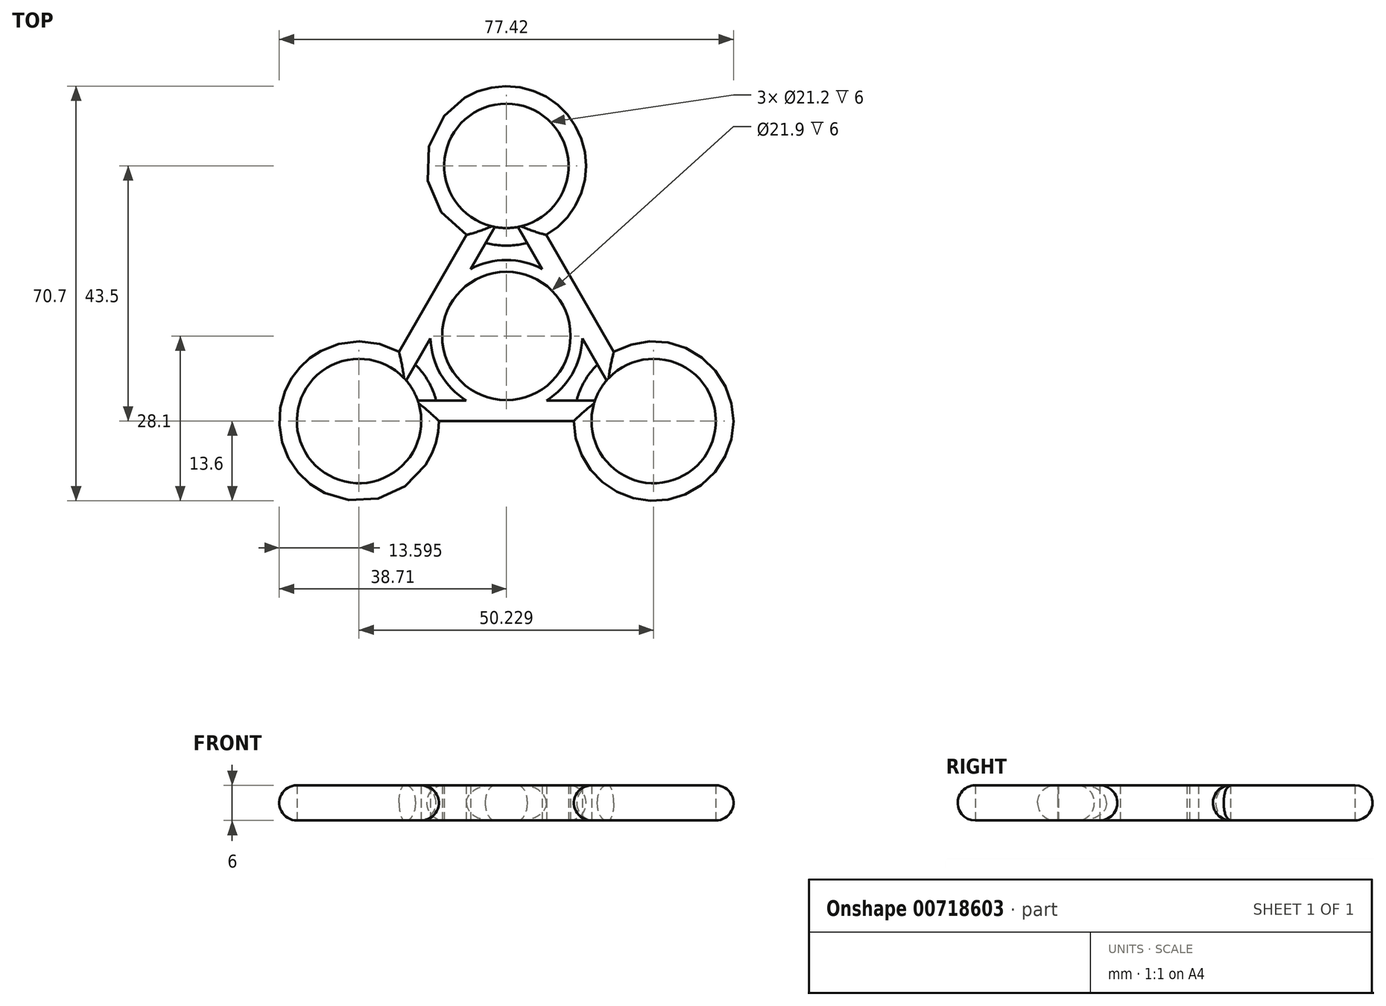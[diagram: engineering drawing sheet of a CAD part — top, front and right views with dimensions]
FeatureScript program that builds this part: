
annotation { "Feature Type Name" : "Feature", "Feature Type Description" : "" }
export const myFeature = defineFeature(function(context is Context, id is Id, definition is map)
    precondition{}
    {
        {
            var Q0;
            Q0=qCreatedBy(makeId("Top.planeOp"),FACE);
            var sketch = newSketch(context, id + "F0", { "sketchPlane" : qUnion([Q0])});
            skCircle(sketch, "E0", {"center": v(0, 0) * mm, "radius": 10.95 * mm});
            skCircle(sketch, "E1.cCircle", {"center": v(0, 0) * mm, "radius": 14.5 * mm, "construction": true});
            skLineSegment(sketch, "E1.0", {"start": v(0, 29) * mm, "end": v(25.11, -14.5) * mm});
            skLineSegment(sketch, "E1.1", {"start": v(25.11, -14.5) * mm, "end": v(-25.11, -14.5) * mm});
            skLineSegment(sketch, "E1.2", {"start": v(-25.11, -14.5) * mm, "end": v(0, 29) * mm});
            skPoint(sketch, "E1.0.midPoint", {"position": v(12.56, 7.25) * mm});
            skCircle(sketch, "E2", {"center": v(0, 29) * mm, "radius": 10.6 * mm});
            skCircle(sketch, "E3", {"center": v(25.11, -14.5) * mm, "radius": 10.6 * mm});
            skCircle(sketch, "E4", {"center": v(-25.11, -14.5) * mm, "radius": 10.6 * mm});
            skCircle(sketch, "E5.0", {"center": v(0, 29) * mm, "radius": 13.6 * mm});
            skCircle(sketch, "E6.0", {"center": v(-25.11, -14.5) * mm, "radius": 13.6 * mm});
            skCircle(sketch, "E7.0", {"center": v(25.11, -14.5) * mm, "radius": 13.6 * mm});
            skLineSegment(sketch, "E8.0", {"start": v(-2.35, 26.06) * mm, "end": v(22.16, -16.39) * mm});
            skLineSegment(sketch, "E9.0", {"start": v(-21.4, -15.06) * mm, "end": v(3.11, 27.39) * mm});
            skLineSegment(sketch, "E10.0", {"start": v(23.75, -11) * mm, "end": v(-25.27, -11) * mm});
            skCircle(sketch, "E11.0", {"center": v(0, 0) * mm, "radius": 12.95 * mm});
            skSolve(sketch);
        }
        {
            var Q0;
            Q0 = qSketchRegion(id + "F0", true);
            var Q1;
            {var subQ0=sQuery(id+"F0.wireOp",EDGE,"E10.0");var subQ1=sQuery(id+"F0.wireOp",EDGE,"E4");var subQ2=makeQuery(id+"F0.imprint","INTERSECT",VERTEX,{"derivedFrom":[subQ1,subQ0]});Q1=makeQuery(id+"F0.imprint","IMPRINT",FACE,{"disambiguationData":[TD([[makeQuery(id+"F0.imprint","IMPRINT",EDGE,{"disambiguationData":[TD([[subQ2,-1.0]])],"derivedFrom":subQ1}),-1.0]])]});}
            var Q2;
            {var subQ0=sQuery(id+"F0.wireOp",EDGE,"E8.0");var subQ1=sQuery(id+"F0.wireOp",EDGE,"E3");var subQ2=makeQuery(id+"F0.imprint","INTERSECT",VERTEX,{"derivedFrom":[subQ1,subQ0]});Q2=makeQuery(id+"F0.imprint","IMPRINT",FACE,{"disambiguationData":[TD([[makeQuery(id+"F0.imprint","IMPRINT",EDGE,{"disambiguationData":[TD([[subQ2,-1.0]])],"derivedFrom":subQ1}),-1.0]])]});}
            var Q3;
            {var subQ0=sQuery(id+"F0.wireOp",EDGE,"E8.0");var subQ1=sQuery(id+"F0.wireOp",EDGE,"E0");var subQ2=makeQuery(id+"F0.imprint","INTERSECT",VERTEX,{"disambiguationData":[OD(1.0)],"derivedFrom":[subQ1,subQ0]});Q3=makeQuery(id+"F0.imprint","IMPRINT",FACE,{"disambiguationData":[TD([[makeQuery(id+"F0.imprint","IMPRINT",EDGE,{"disambiguationData":[TD([[subQ2,1.0]])],"derivedFrom":subQ1}),-1.0]])]});}
            var Q4;
            {var subQ0=sQuery(id+"F0.wireOp",EDGE,"E9.0");var subQ1=sQuery(id+"F0.wireOp",EDGE,"E0");var subQ2=makeQuery(id+"F0.imprint","INTERSECT",VERTEX,{"disambiguationData":[OD(1.0)],"derivedFrom":[subQ1,subQ0]});Q4=makeQuery(id+"F0.imprint","IMPRINT",FACE,{"disambiguationData":[TD([[makeQuery(id+"F0.imprint","IMPRINT",EDGE,{"disambiguationData":[TD([[subQ2,-1.0]])],"derivedFrom":subQ1}),-1.0]])]});}
            var Q5;
            {var subQ0=sQuery(id+"F0.wireOp",EDGE,"E8.0");var subQ1=sQuery(id+"F0.wireOp",EDGE,"E0");var subQ2=makeQuery(id+"F0.imprint","INTERSECT",VERTEX,{"disambiguationData":[OD(0.0)],"derivedFrom":[subQ1,subQ0]});Q5=makeQuery(id+"F0.imprint","IMPRINT",FACE,{"disambiguationData":[TD([[makeQuery(id+"F0.imprint","IMPRINT",EDGE,{"disambiguationData":[TD([[subQ2,-1.0]])],"derivedFrom":subQ1}),-1.0]])]});}
            var Q6;
            {var subQ0=sQuery(id+"F0.wireOp",EDGE,"E9.0");var subQ1=sQuery(id+"F0.wireOp",EDGE,"E2");var subQ2=makeQuery(id+"F0.imprint","INTERSECT",VERTEX,{"derivedFrom":[subQ1,subQ0]});Q6=makeQuery(id+"F0.imprint","IMPRINT",FACE,{"disambiguationData":[TD([[makeQuery(id+"F0.imprint","IMPRINT",EDGE,{"disambiguationData":[TD([[subQ2,-1.0]])],"derivedFrom":subQ1}),-1.0]])]});}
            var Q7;
            {var subQ0=sQuery(id+"F0.wireOp",EDGE,"E9.0");var subQ1=sQuery(id+"F0.wireOp",EDGE,"E0");var subQ2=makeQuery(id+"F0.imprint","INTERSECT",VERTEX,{"disambiguationData":[OD(0.0)],"derivedFrom":[subQ1,subQ0]});Q7=makeQuery(id+"F0.imprint","IMPRINT",FACE,{"disambiguationData":[TD([[makeQuery(id+"F0.imprint","IMPRINT",EDGE,{"disambiguationData":[TD([[subQ2,-1.0]])],"derivedFrom":subQ1}),-1.0]])]});}
            var Q8;
            {var subQ0=sQuery(id+"F0.wireOp",EDGE,"E10.0");var subQ1=sQuery(id+"F0.wireOp",EDGE,"E0");var subQ2=makeQuery(id+"F0.imprint","INTERSECT",VERTEX,{"disambiguationData":[OD(0.0)],"derivedFrom":[subQ1,subQ0]});Q8=makeQuery(id+"F0.imprint","IMPRINT",FACE,{"disambiguationData":[TD([[makeQuery(id+"F0.imprint","IMPRINT",EDGE,{"disambiguationData":[TD([[subQ2,-1.0]])],"derivedFrom":subQ1}),-1.0]])]});}
            var Q9;
            {var subQ0=sQuery(id+"F0.wireOp",EDGE,"E8.0");var subQ1=sQuery(id+"F0.wireOp",EDGE,"E0");var subQ2=makeQuery(id+"F0.imprint","INTERSECT",VERTEX,{"disambiguationData":[OD(0.0)],"derivedFrom":[subQ1,subQ0]});Q9=makeQuery(id+"F0.imprint","IMPRINT",FACE,{"disambiguationData":[TD([[makeQuery(id+"F0.imprint","IMPRINT",EDGE,{"disambiguationData":[TD([[subQ2,1.0]])],"derivedFrom":subQ1}),-1.0]])]});}
            var Q10;
            {var subQ0=sQuery(id+"F0.wireOp",EDGE,"E11.0");var subQ1=sQuery(id+"F0.wireOp",EDGE,"E8.0");var subQ2=makeQuery(id+"F0.imprint","INTERSECT",VERTEX,{"disambiguationData":[OD(0.0)],"derivedFrom":[subQ1,subQ0]});Q10=makeQuery(id+"F0.imprint","IMPRINT",FACE,{"disambiguationData":[TD([[makeQuery(id+"F0.imprint","IMPRINT",EDGE,{"disambiguationData":[TD([[subQ2,-1.0]])],"derivedFrom":subQ1}),1.0]])]});}
            var Q11;
            Q11=makeQuery(id+"F0.imprint","IMPRINT",FACE,{"disambiguationData":[TD([[makeQuery(id+"F0.imprint","IMPRINT",EDGE,{"derivedFrom":sQuery(id+"F0.wireOp",EDGE,"E0")}),-1.0]])]});
            var Q12;
            {var subQ0=sQuery(id+"F0.wireOp",EDGE,"E11.0");var subQ1=sQuery(id+"F0.wireOp",EDGE,"E9.0");var subQ2=makeQuery(id+"F0.imprint","INTERSECT",VERTEX,{"disambiguationData":[OD(0.0)],"derivedFrom":[subQ1,subQ0]});Q12=makeQuery(id+"F0.imprint","IMPRINT",FACE,{"disambiguationData":[TD([[makeQuery(id+"F0.imprint","IMPRINT",EDGE,{"disambiguationData":[TD([[subQ2,-1.0]])],"derivedFrom":subQ1}),1.0]])]});}
            var Q13;
            {var subQ0=sQuery(id+"F0.wireOp",EDGE,"E11.0");var subQ1=sQuery(id+"F0.wireOp",EDGE,"E10.0");var subQ2=makeQuery(id+"F0.imprint","INTERSECT",VERTEX,{"disambiguationData":[OD(0.0)],"derivedFrom":[subQ1,subQ0]});Q13=makeQuery(id+"F0.imprint","IMPRINT",FACE,{"disambiguationData":[TD([[makeQuery(id+"F0.imprint","IMPRINT",EDGE,{"disambiguationData":[TD([[subQ2,-1.0]])],"derivedFrom":subQ1}),1.0]])]});}
            extrude(context, id + "F1", {"entities" : qUnion([Q0, Q1, Q2, Q3, Q4, Q5, Q6, Q7, Q8, Q9, Q10, Q11, Q12, Q13]), "depth" : 6 * mm, "offsetDistance" : 25 * mm});
        }
        {
            var Q0;
            {var subQ0=sQuery(id+"F0.wireOp",EDGE,"E6.0");Q0=makeQuery(id+"F1.opExtrude","CAP_EDGE",EDGE,{"disambiguationData":[OSD([subQ0]),TDD([makeQuery(id+"F0.imprint","IMPRINT",EDGE,{"disambiguationData":[TD([[makeQuery(id+"F0.imprint","INTERSECT",VERTEX,{"derivedFrom":[sQuery(id+"F0.wireOp",EDGE,"E1.1"),subQ0]}),1.0]])],"derivedFrom":subQ0})])],"isStart":false});}
            var Q1;
            {var subQ0=sQuery(id+"F0.wireOp",EDGE,"E7.0");Q1=makeQuery(id+"F1.opExtrude","CAP_EDGE",EDGE,{"disambiguationData":[OSD([subQ0]),TDD([makeQuery(id+"F0.imprint","IMPRINT",EDGE,{"disambiguationData":[TD([[makeQuery(id+"F0.imprint","INTERSECT",VERTEX,{"derivedFrom":[sQuery(id+"F0.wireOp",EDGE,"E1.0"),subQ0]}),1.0]])],"derivedFrom":subQ0})])],"isStart":false});}
            var Q2;
            {var subQ0=sQuery(id+"F0.wireOp",EDGE,"E5.0");Q2=makeQuery(id+"F1.opExtrude","CAP_EDGE",EDGE,{"disambiguationData":[OSD([subQ0]),TDD([makeQuery(id+"F0.imprint","IMPRINT",EDGE,{"disambiguationData":[TD([[makeQuery(id+"F0.imprint","INTERSECT",VERTEX,{"derivedFrom":[sQuery(id+"F0.wireOp",EDGE,"E1.0"),subQ0]}),-1.0]])],"derivedFrom":subQ0})])],"isStart":false});}
            var Q3;
            Q3=makeQuery(id+"F1.opExtrude","CAP_EDGE",EDGE,{"disambiguationData":[OSD([sQuery(id+"F0.wireOp",EDGE,"E1.1")])],"isStart":false});
            var Q4;
            Q4=makeQuery(id+"F1.opExtrude","CAP_EDGE",EDGE,{"disambiguationData":[OSD([sQuery(id+"F0.wireOp",EDGE,"E1.0")])],"isStart":false});
            var Q5;
            Q5=makeQuery(id+"F1.opExtrude","CAP_EDGE",EDGE,{"disambiguationData":[OSD([sQuery(id+"F0.wireOp",EDGE,"E1.2")])],"isStart":false});
            var Q6;
            {var subQ0=sQuery(id+"F0.wireOp",EDGE,"E6.0");Q6=makeQuery(id+"F1.opExtrude","CAP_EDGE",EDGE,{"disambiguationData":[OSD([subQ0]),TDD([makeQuery(id+"F0.imprint","IMPRINT",EDGE,{"disambiguationData":[TD([[makeQuery(id+"F0.imprint","INTERSECT",VERTEX,{"derivedFrom":[subQ0,sQuery(id+"F0.wireOp",EDGE,"E10.0")]}),-1.0]])],"derivedFrom":subQ0})])],"isStart":false});}
            var Q7;
            {var subQ0=sQuery(id+"F0.wireOp",EDGE,"E6.0");Q7=makeQuery(id+"F1.opExtrude","CAP_EDGE",EDGE,{"disambiguationData":[OSD([subQ0]),TDD([makeQuery(id+"F0.imprint","IMPRINT",EDGE,{"disambiguationData":[TD([[makeQuery(id+"F0.imprint","INTERSECT",VERTEX,{"derivedFrom":[sQuery(id+"F0.wireOp",EDGE,"E1.1"),subQ0]}),1.0]])],"derivedFrom":subQ0})])],"isStart":true});}
            var Q8;
            Q8=makeQuery(id+"F1.opExtrude","CAP_EDGE",EDGE,{"disambiguationData":[OSD([sQuery(id+"F0.wireOp",EDGE,"E1.1")])],"isStart":true});
            var Q9;
            {var subQ0=sQuery(id+"F0.wireOp",EDGE,"E7.0");Q9=makeQuery(id+"F1.opExtrude","CAP_EDGE",EDGE,{"disambiguationData":[OSD([subQ0]),TDD([makeQuery(id+"F0.imprint","IMPRINT",EDGE,{"disambiguationData":[TD([[makeQuery(id+"F0.imprint","INTERSECT",VERTEX,{"derivedFrom":[sQuery(id+"F0.wireOp",EDGE,"E1.0"),subQ0]}),1.0]])],"derivedFrom":subQ0})])],"isStart":true});}
            var Q10;
            Q10=makeQuery(id+"F1.opExtrude","CAP_EDGE",EDGE,{"disambiguationData":[OSD([sQuery(id+"F0.wireOp",EDGE,"E1.0")])],"isStart":true});
            var Q11;
            {var subQ0=sQuery(id+"F0.wireOp",EDGE,"E5.0");Q11=makeQuery(id+"F1.opExtrude","CAP_EDGE",EDGE,{"disambiguationData":[OSD([subQ0]),TDD([makeQuery(id+"F0.imprint","IMPRINT",EDGE,{"disambiguationData":[TD([[makeQuery(id+"F0.imprint","INTERSECT",VERTEX,{"derivedFrom":[sQuery(id+"F0.wireOp",EDGE,"E1.0"),subQ0]}),-1.0]])],"derivedFrom":subQ0})])],"isStart":true});}
            var Q12;
            Q12=makeQuery(id+"F1.opExtrude","CAP_EDGE",EDGE,{"disambiguationData":[OSD([sQuery(id+"F0.wireOp",EDGE,"E1.2")])],"isStart":true});
            var Q13;
            {var subQ0=sQuery(id+"F0.wireOp",EDGE,"E7.0");Q13=makeQuery(id+"F1.opExtrude","CAP_EDGE",EDGE,{"disambiguationData":[OSD([subQ0]),TDD([makeQuery(id+"F0.imprint","IMPRINT",EDGE,{"disambiguationData":[TD([[makeQuery(id+"F0.imprint","INTERSECT",VERTEX,{"derivedFrom":[subQ0,sQuery(id+"F0.wireOp",EDGE,"E8.0")]}),-1.0]])],"derivedFrom":subQ0})])],"isStart":false});}
            var Q14;
            {var subQ0=sQuery(id+"F0.wireOp",EDGE,"E5.0");Q14=makeQuery(id+"F1.opExtrude","CAP_EDGE",EDGE,{"disambiguationData":[OSD([subQ0]),TDD([makeQuery(id+"F0.imprint","IMPRINT",EDGE,{"disambiguationData":[TD([[makeQuery(id+"F0.imprint","INTERSECT",VERTEX,{"derivedFrom":[subQ0,sQuery(id+"F0.wireOp",EDGE,"E9.0")]}),-1.0]])],"derivedFrom":subQ0})])],"isStart":false});}
            var Q15;
            {var subQ0=sQuery(id+"F0.wireOp",EDGE,"E5.0");Q15=makeQuery(id+"F1.opExtrude","CAP_EDGE",EDGE,{"disambiguationData":[OSD([subQ0]),TDD([makeQuery(id+"F0.imprint","IMPRINT",EDGE,{"disambiguationData":[TD([[makeQuery(id+"F0.imprint","INTERSECT",VERTEX,{"derivedFrom":[subQ0,sQuery(id+"F0.wireOp",EDGE,"E9.0")]}),-1.0]])],"derivedFrom":subQ0})])],"isStart":true});}
            var Q16;
            {var subQ0=sQuery(id+"F0.wireOp",EDGE,"E7.0");Q16=makeQuery(id+"F1.opExtrude","CAP_EDGE",EDGE,{"disambiguationData":[OSD([subQ0]),TDD([makeQuery(id+"F0.imprint","IMPRINT",EDGE,{"disambiguationData":[TD([[makeQuery(id+"F0.imprint","INTERSECT",VERTEX,{"derivedFrom":[subQ0,sQuery(id+"F0.wireOp",EDGE,"E8.0")]}),-1.0]])],"derivedFrom":subQ0})])],"isStart":true});}
            var Q17;
            {var subQ0=sQuery(id+"F0.wireOp",EDGE,"E6.0");Q17=makeQuery(id+"F1.opExtrude","CAP_EDGE",EDGE,{"disambiguationData":[OSD([subQ0]),TDD([makeQuery(id+"F0.imprint","IMPRINT",EDGE,{"disambiguationData":[TD([[makeQuery(id+"F0.imprint","INTERSECT",VERTEX,{"derivedFrom":[subQ0,sQuery(id+"F0.wireOp",EDGE,"E10.0")]}),-1.0]])],"derivedFrom":subQ0})])],"isStart":true});}
            fillet(context, id + "F2", {"entities" : qUnion([Q0, Q1, Q2, Q3, Q4, Q5, Q6, Q7, Q8, Q9, Q10, Q11, Q12, Q13, Q14, Q15, Q16, Q17]), "radius" : 3 * mm, "tangentPropagation" : true, "allowEdgeOverflow" : false});
        }
    });
